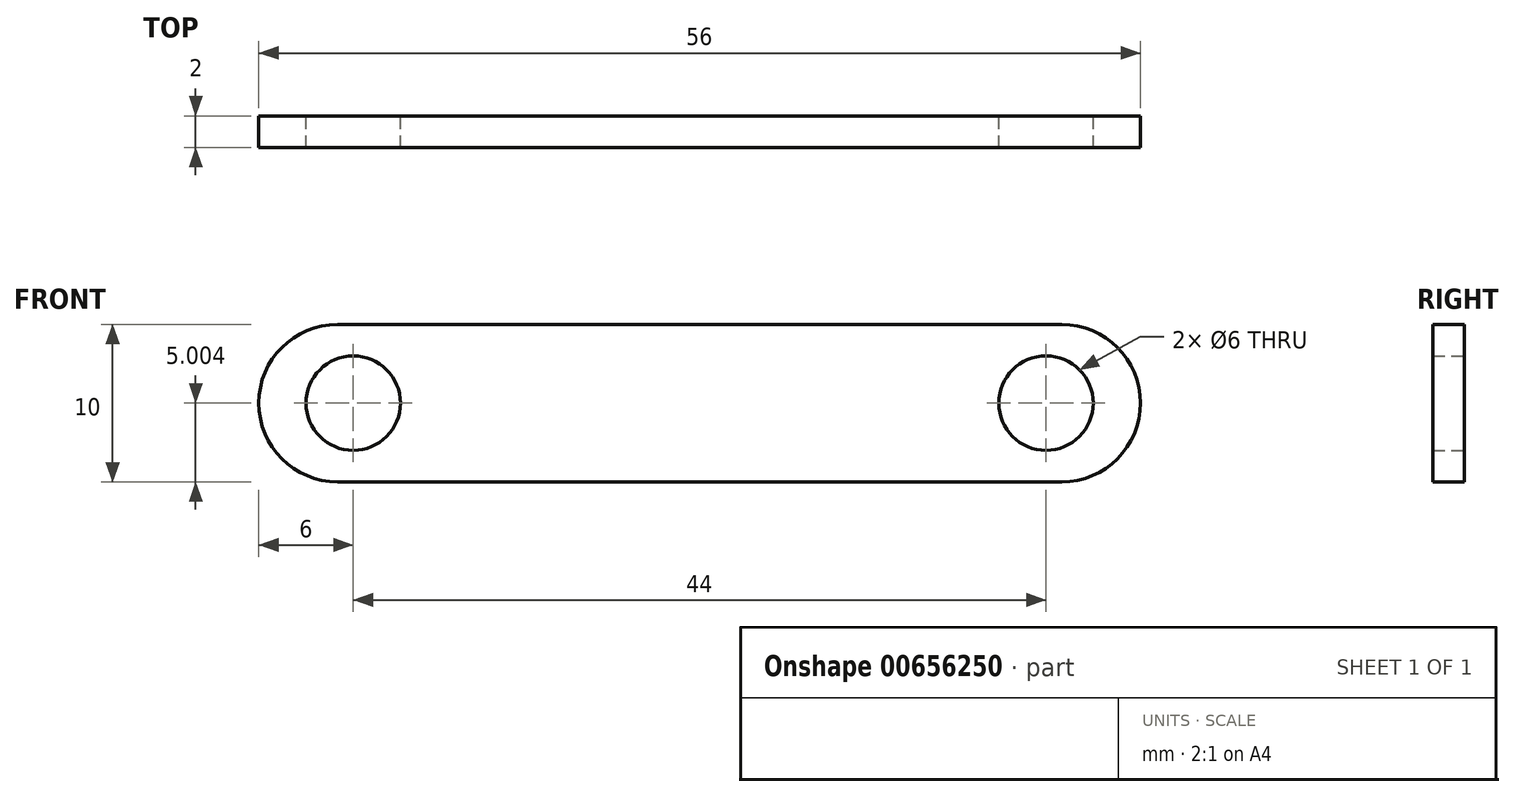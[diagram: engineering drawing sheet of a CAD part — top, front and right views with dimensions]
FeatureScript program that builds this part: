
annotation { "Feature Type Name" : "Feature", "Feature Type Description" : "" }
export const myFeature = defineFeature(function(context is Context, id is Id, definition is map)
    precondition{}
    {
        {
            var Q0;
            Q0=qCreatedBy(makeId("Front.planeOp"),FACE);
            var sketch = newSketch(context, id + "F0", { "sketchPlane" : qUnion([Q0])});
            skLineSegment(sketch, "E0.bottom", {"start": v(-49.84, 5.24) * mm, "end": v(6.16, 5.24) * mm});
            skLineSegment(sketch, "E0.top", {"start": v(-49.84, -4.76) * mm, "end": v(6.16, -4.76) * mm});
            skLineSegment(sketch, "E0.left", {"start": v(-49.84, 5.24) * mm, "end": v(-49.84, -4.76) * mm});
            skLineSegment(sketch, "E0.right", {"start": v(6.16, 5.24) * mm, "end": v(6.16, -4.76) * mm});
            skCircle(sketch, "E1", {"center": v(0.16, 0.24) * mm, "radius": 3 * mm});
            skCircle(sketch, "E2", {"center": v(-43.84, 0.24) * mm, "radius": 3 * mm});
            skPoint(sketch, "E2.centerSnap0", {"position": v(-49.84, 0.24) * mm});
            skSolve(sketch);
        }
        {
            var Q0;
            Q0 = qSketchRegion(id + "F0", true);
            extrude(context, id + "F1", {"entities" : qUnion([Q0]), "depth" : 2 * mm, "offsetDistance" : 25 * mm});
        }
        {
            var Q0;
            Q0=makeQuery(id+"F1.opExtrude","SWEPT_EDGE",EDGE,{"disambiguationData":[OSD([sQuery(id+"F0.wireOp",EDGE,"E0.bottom"),sQuery(id+"F0.wireOp",EDGE,"E0.left")])]});
            var Q1;
            Q1=makeQuery(id+"F1.opExtrude","SWEPT_EDGE",EDGE,{"disambiguationData":[OSD([sQuery(id+"F0.wireOp",EDGE,"E0.top"),sQuery(id+"F0.wireOp",EDGE,"E0.left")])]});
            var Q2;
            Q2=makeQuery(id+"F1.opExtrude","SWEPT_EDGE",EDGE,{"disambiguationData":[OSD([sQuery(id+"F0.wireOp",EDGE,"E0.bottom"),sQuery(id+"F0.wireOp",EDGE,"E0.right")])]});
            var Q3;
            Q3=makeQuery(id+"F1.opExtrude","SWEPT_EDGE",EDGE,{"disambiguationData":[OSD([sQuery(id+"F0.wireOp",EDGE,"E0.top"),sQuery(id+"F0.wireOp",EDGE,"E0.right")])]});
            fillet(context, id + "F2", {"entities" : qUnion([Q0, Q1, Q2, Q3]), "radius" : 5 * mm, "tangentPropagation" : true, "allowEdgeOverflow" : false});
        }
    });
